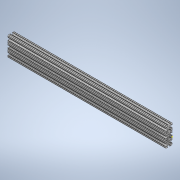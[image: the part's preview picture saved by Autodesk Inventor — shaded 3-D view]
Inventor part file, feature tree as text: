
AUTODESK INVENTOR PART (.ipt)
format: ipt  version: 2020 (Build 240168000, 168)  size: 381,440 bytes
history: native  units: in
note: dims shown in document units (in); Inventor stores cm internally (conversion verified against a paired STEP export)
features: sketch x2, extrude x1
ambient origin geometry x8: Origin, YZ Plane, XZ Plane, XY Plane, X Axis, Y Axis, Z Axis, Center Point
bodies: Solid1 (feature_tree)
feature tree (3):
  extrude  "Extrusion1"  [1 undecoded]
  sketch  "Sketch2"
  sketch  "Sketch1"  dims[d0=24.0in d1=0.0in]
note: 1 required parameter value undecoded (feature->parameter linkage not recoverable at this tier; creation-order binding heuristic only, values carry confidence <= 0.55)
